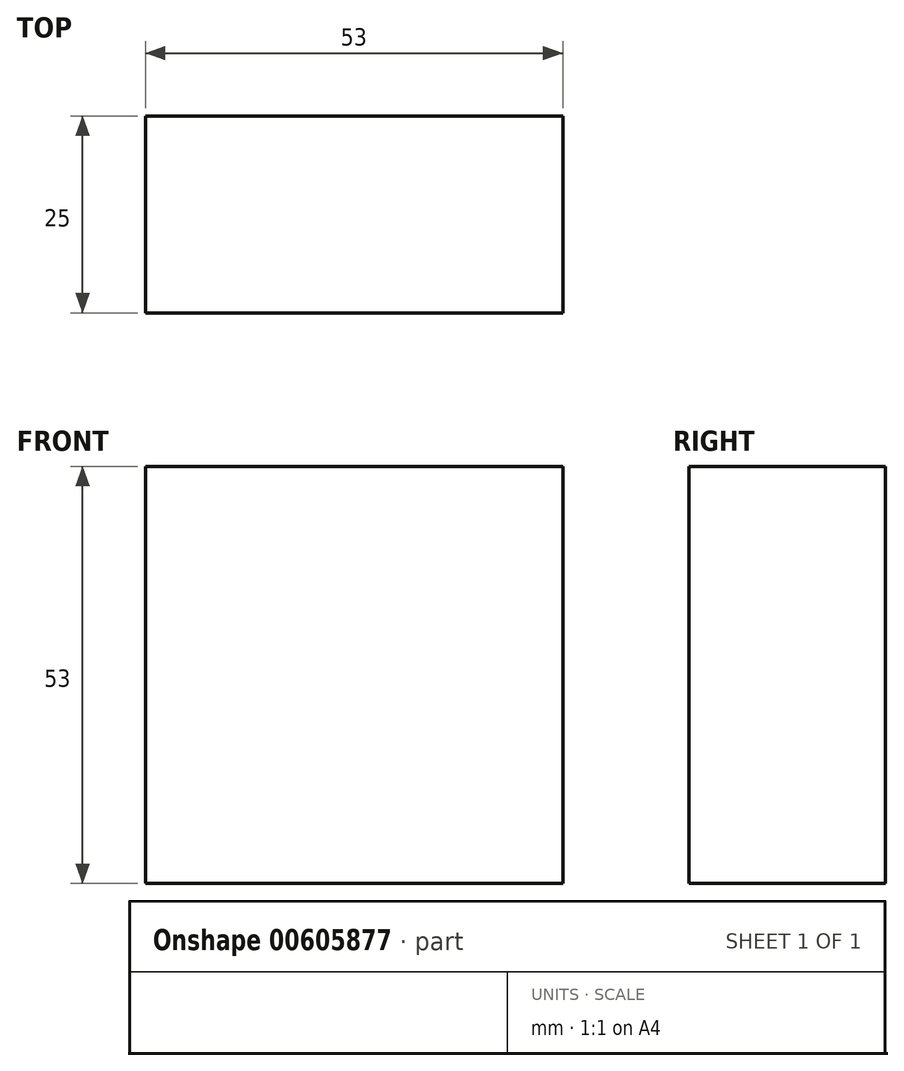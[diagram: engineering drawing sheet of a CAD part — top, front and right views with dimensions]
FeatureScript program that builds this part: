
annotation { "Feature Type Name" : "Feature", "Feature Type Description" : "" }
export const myFeature = defineFeature(function(context is Context, id is Id, definition is map)
    precondition{}
    {
        {
            var Q0;
            Q0=qCreatedBy(makeId("Front.planeOp"),FACE);
            var sketch = newSketch(context, id + "F0", { "sketchPlane" : qUnion([Q0])});
            skLineSegment(sketch, "E0", {"start": v(-26.35, 27.93) * mm, "end": v(26.65, 27.93) * mm});
            skLineSegment(sketch, "E1", {"start": v(-26.35, 27.93) * mm, "end": v(-26.35, -25.07) * mm});
            skLineSegment(sketch, "E2", {"start": v(-26.35, -25.07) * mm, "end": v(26.65, -25.07) * mm});
            skLineSegment(sketch, "E3", {"start": v(26.65, 27.93) * mm, "end": v(26.65, -25.07) * mm});
            skSolve(sketch);
        }
        {
            var Q0;
            Q0 = qSketchRegion(id + "F0", true);
            extrude(context, id + "F1", {"entities" : qUnion([Q0]), "depth" : 25 * mm, "offsetDistance" : 25 * mm});
        }
    });
